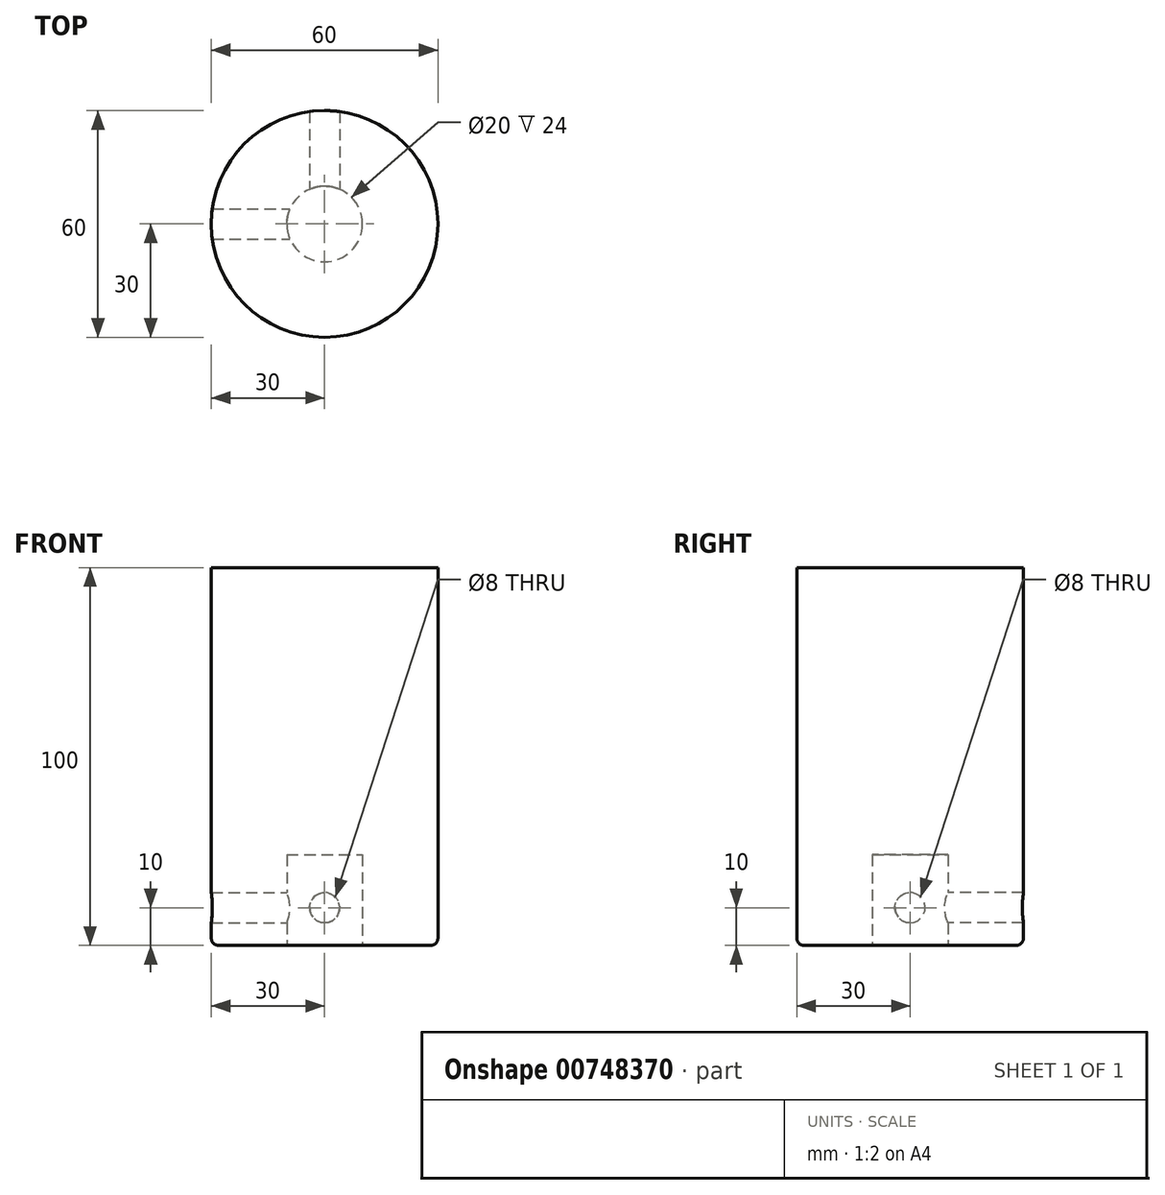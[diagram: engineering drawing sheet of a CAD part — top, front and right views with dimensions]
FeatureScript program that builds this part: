
annotation { "Feature Type Name" : "Feature", "Feature Type Description" : "" }
export const myFeature = defineFeature(function(context is Context, id is Id, definition is map)
    precondition{}
    {
        {
            var Q0;
            Q0=qCreatedBy(makeId("Top.planeOp"),FACE);
            var sketch = newSketch(context, id + "F0", { "sketchPlane" : qUnion([Q0])});
            skCircle(sketch, "E0", {"center": v(0, 0) * mm, "radius": 30 * mm});
            skSolve(sketch);
        }
        {
            var Q0;
            Q0=makeQuery(id+"F0.imprint","IMPRINT",FACE,{"disambiguationData":[TD([[makeQuery(id+"F0.imprint","IMPRINT",EDGE,{"derivedFrom":sQuery(id+"F0.wireOp",EDGE,"E0")}),1.0]])]});
            extrude(context, id + "F1", {"entities" : qUnion([Q0]), "depth" : 100 * mm, "offsetDistance" : 25 * mm});
        }
        {
            var Q0;
            Q0=makeQuery(id+"F1.opExtrude","CAP_FACE",FACE,{"disambiguationData":[OSD([sQuery(id+"F0.wireOp",EDGE,"E0")])],"isStart":true});
            var sketch = newSketch(context, id + "F2", { "sketchPlane" : qUnion([Q0])});
            skCircle(sketch, "E1", {"center": v(0, 0) * mm, "radius": 10 * mm});
            skSolve(sketch);
        }
        {
            var Q0;
            Q0 = qSketchRegion(id + "F2", true);
            extrude(context, id + "F3", {"entities" : qUnion([Q0]), "operationType" : NewBodyOperationType.REMOVE, "oppositeDirection" : true, "depth" : 24 * mm, "offsetDistance" : 25 * mm});
        }
        {
            var Q0;
            Q0=makeQuery(id+"F3.boolean.opBoolean","COPY",EDGE,{"derivedFrom":makeQuery(id+"F3.opExtrude","CAP_EDGE",EDGE,{"disambiguationData":[OSD([sQuery(id+"F2.wireOp",EDGE,"E1")])],"isStart":true})});
            var Q1;
            Q1=makeQuery(id+"F1.opExtrude","CAP_EDGE",EDGE,{"disambiguationData":[OSD([sQuery(id+"F0.wireOp",EDGE,"E0")])],"isStart":true});
            fillet(context, id + "F4", {"entities" : qUnion([Q0, Q1]), "radius" : 2 * mm, "tangentPropagation" : true, "allowEdgeOverflow" : false});
        }
        {
            var Q0;
            Q0=qCreatedBy(makeId("Right.planeOp"),FACE);
            var sketch = newSketch(context, id + "F5", { "sketchPlane" : qUnion([Q0])});
            skCircle(sketch, "E2", {"center": v(0, 10) * mm, "radius": 4 * mm});
            skSolve(sketch);
        }
        {
            var Q0;
            Q0 = qSketchRegion(id + "F5", true);
            extrude(context, id + "F6", {"entities" : qUnion([Q0]), "operationType" : NewBodyOperationType.REMOVE, "oppositeDirection" : true, "depth" : 30 * mm, "offsetDistance" : 25 * mm});
        }
        {
            var Q0;
            Q0=qCreatedBy(makeId("Front.planeOp"),FACE);
            var sketch = newSketch(context, id + "F7", { "sketchPlane" : qUnion([Q0])});
            skCircle(sketch, "E3", {"center": v(0, 10) * mm, "radius": 4 * mm});
            skSolve(sketch);
        }
        {
            var Q0;
            Q0 = qSketchRegion(id + "F7", true);
            extrude(context, id + "F8", {"entities" : qUnion([Q0]), "operationType" : NewBodyOperationType.REMOVE, "oppositeDirection" : true, "depth" : 30 * mm, "offsetDistance" : 25 * mm});
        }
    });
